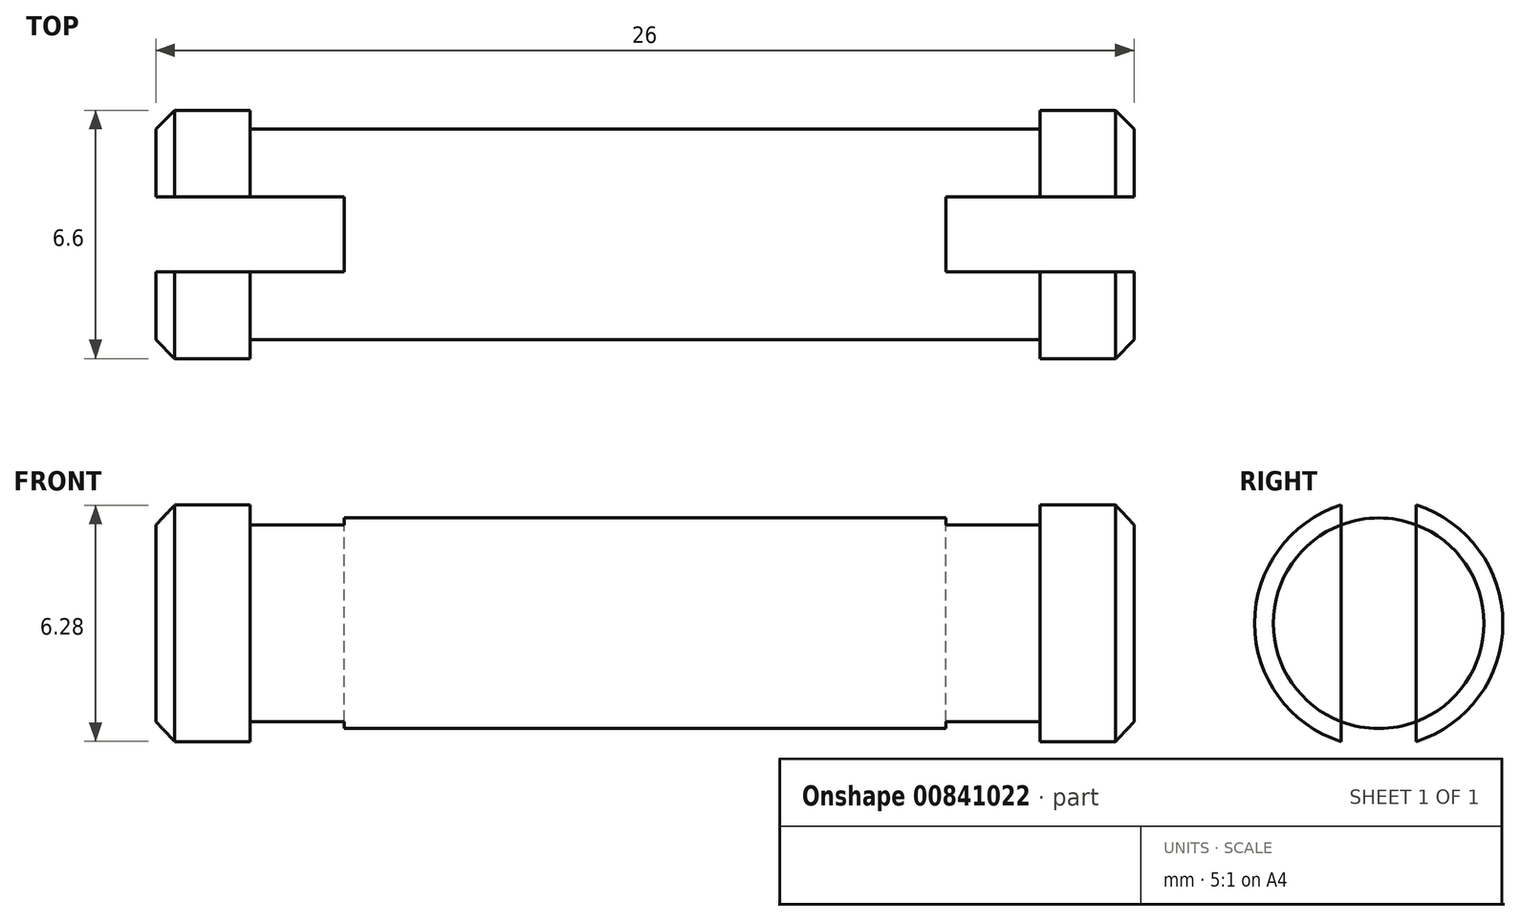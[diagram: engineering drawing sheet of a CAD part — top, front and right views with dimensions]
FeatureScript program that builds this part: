
annotation { "Feature Type Name" : "Feature", "Feature Type Description" : "" }
export const myFeature = defineFeature(function(context is Context, id is Id, definition is map)
    precondition{}
    {
        {
            var Q0;
            Q0=qCreatedBy(makeId("Front.planeOp"),FACE);
            var sketch = newSketch(context, id + "F0", { "sketchPlane" : qUnion([Q0])});
            skLineSegment(sketch, "E0", {"start": v(-7.06, 0) * mm, "end": v(18.94, 0) * mm});
            skLineSegment(sketch, "E1", {"start": v(18.94, 0) * mm, "end": v(18.94, 2.8) * mm});
            skLineSegment(sketch, "E2", {"start": v(18.94, 2.8) * mm, "end": v(18.44, 3.3) * mm});
            skLineSegment(sketch, "E3", {"start": v(18.44, 3.3) * mm, "end": v(16.44, 3.3) * mm});
            skLineSegment(sketch, "E4", {"start": v(16.44, 3.3) * mm, "end": v(16.44, 2.8) * mm});
            skLineSegment(sketch, "E5", {"start": v(16.44, 2.8) * mm, "end": v(-4.56, 2.8) * mm});
            skLineSegment(sketch, "E6", {"start": v(-4.56, 2.8) * mm, "end": v(-4.56, 3.3) * mm});
            skLineSegment(sketch, "E7", {"start": v(-4.56, 3.3) * mm, "end": v(-6.56, 3.3) * mm});
            skLineSegment(sketch, "E8", {"start": v(-6.56, 3.3) * mm, "end": v(-7.06, 2.8) * mm});
            skLineSegment(sketch, "E9", {"start": v(-7.06, 2.8) * mm, "end": v(-7.06, 0) * mm});
            skSolve(sketch);
        }
        {
            var Q0;
            Q0=makeQuery(id+"F0.imprint","IMPRINT",FACE,{"disambiguationData":[TD([[makeQuery(id+"F0.imprint","IMPRINT",EDGE,{"derivedFrom":sQuery(id+"F0.wireOp",EDGE,"E0")}),1.0]])]});
            var Q1;
            Q1=sQuery(id+"F0.wireOp",EDGE,"E0");
            revolve(context, id + "F1", {"surfaceOperationType" : NewSurfaceOperationType.NEW, "entities" : qUnion([Q0]), "axis" : qUnion([Q1]), "revolveType" : RevolveType.FULL});
        }
        {
            var Q0;
            Q0=qCreatedBy(makeId("Top.planeOp"),FACE);
            var sketch = newSketch(context, id + "F2", { "sketchPlane" : qUnion([Q0])});
            skLineSegment(sketch, "E10.bottom", {"start": v(-8.73, 1) * mm, "end": v(-2.06, 1) * mm});
            skLineSegment(sketch, "E10.top", {"start": v(-8.73, -1) * mm, "end": v(-2.06, -1) * mm});
            skLineSegment(sketch, "E10.left", {"start": v(-8.73, 1) * mm, "end": v(-8.73, -1) * mm});
            skLineSegment(sketch, "E10.right", {"start": v(-2.06, 1) * mm, "end": v(-2.06, -1) * mm});
            skLineSegment(sketch, "E11.bottom", {"start": v(13.94, 1) * mm, "end": v(28.77, 1) * mm});
            skLineSegment(sketch, "E11.top", {"start": v(13.94, -1) * mm, "end": v(28.77, -1) * mm});
            skLineSegment(sketch, "E11.left", {"start": v(13.94, 1) * mm, "end": v(13.94, -1) * mm});
            skLineSegment(sketch, "E11.right", {"start": v(28.77, 1) * mm, "end": v(28.77, -1) * mm});
            skSolve(sketch);
        }
        {
            var Q0;
            Q0=qSketchRegion(id+"F2",true);
            extrude(context, id + "F3", {"entities" : qUnion([Q0]), "operationType" : NewBodyOperationType.REMOVE, "endBound" : BoundingType.SYMMETRIC, "oppositeDirection" : true, "depth" : 25 * mm, "offsetDistance" : 25 * mm});
        }
    });
